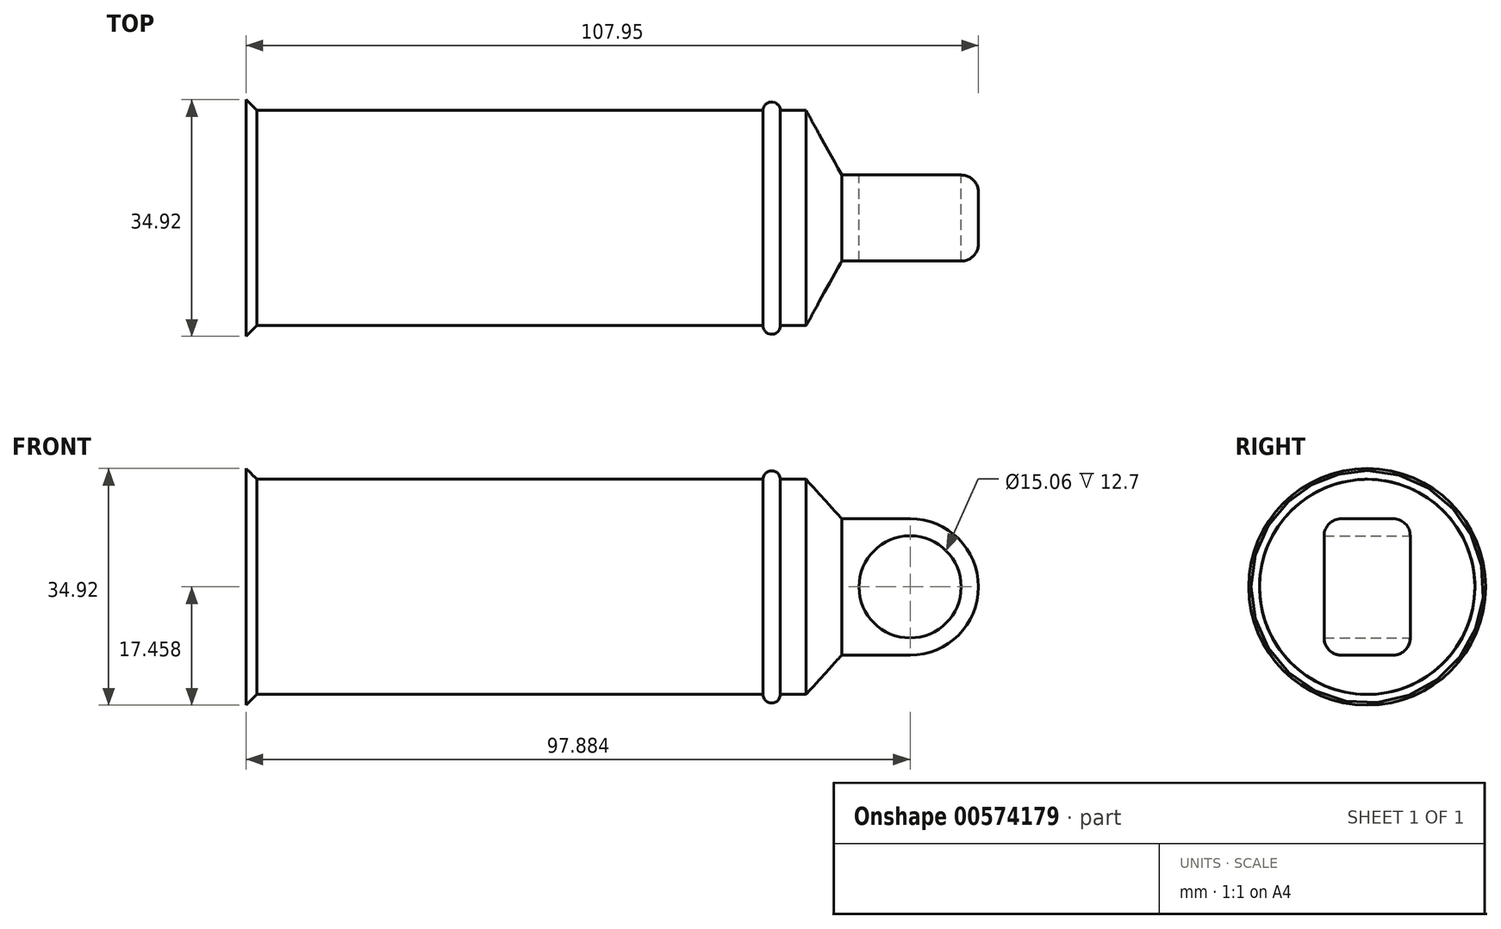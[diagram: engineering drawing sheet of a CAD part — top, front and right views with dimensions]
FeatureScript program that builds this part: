
annotation { "Feature Type Name" : "Feature", "Feature Type Description" : "" }
export const myFeature = defineFeature(function(context is Context, id is Id, definition is map)
    precondition{}
    {
        {
            var Q0;
            Q0=qCreatedBy(makeId("Front.planeOp"),FACE);
            var sketch = newSketch(context, id + "F0", { "sketchPlane" : qUnion([Q0])});
            skLineSegment(sketch, "E0", {"start": v(-107.03, -17.15) * mm, "end": v(134.27, -17.15) * mm, "construction": true});
            skCircle(sketch, "E1", {"center": v(-107.03, -17.15) * mm, "radius": 7.53 * mm});
            skCircle(sketch, "E2", {"center": v(134.27, -17.15) * mm, "radius": 7.53 * mm});
            skArc(sketch, "E3.0", {"start": v(-112.09, -8.45) * mm, "mid": v(-117.1, -17.15) * mm, "end": v(-112.09, -25.86) * mm});
            skArc(sketch, "E4.0", {"start": v(134.27, -27.22) * mm, "mid": v(144.34, -17.15) * mm, "end": v(134.27, -7.08) * mm});
            skLineSegment(sketch, "E5", {"start": v(134.27, -7.08) * mm, "end": v(118.94, -7.08) * mm});
            skLineSegment(sketch, "E6", {"start": v(118.94, -17.15) * mm, "end": v(118.94, -1.28) * mm});
            skLineSegment(sketch, "E7", {"start": v(118.94, -1.28) * mm, "end": v(115.13, -1.28) * mm});
            skLineSegment(sketch, "E8", {"start": v(36.4, -1.28) * mm, "end": v(36.4, -17.15) * mm});
            skLineSegment(sketch, "E9", {"start": v(115.13, -0.97) * mm, "end": v(115.13, -1.28) * mm});
            skLineSegment(sketch, "E10", {"start": v(112.6, -1.28) * mm, "end": v(112.6, -0.97) * mm});
            skLineSegment(sketch, "E11.trimOffspring", {"start": v(112.6, -1.28) * mm, "end": v(37.98, -1.28) * mm});
            skLineSegment(sketch, "E12", {"start": v(36.4, -1.28) * mm, "end": v(36.4, 1.9) * mm});
            skLineSegment(sketch, "E13", {"start": v(35.12, 1.9) * mm, "end": v(27.44, 1.9) * mm});
            skLineSegment(sketch, "E14", {"start": v(27.44, 1.9) * mm, "end": v(27.44, 4.44) * mm});
            skLineSegment(sketch, "E15", {"start": v(27.44, 4.44) * mm, "end": v(-53.08, 4.44) * mm});
            skLineSegment(sketch, "E16", {"start": v(-53.08, 4.44) * mm, "end": v(-53.08, 9.26) * mm});
            skLineSegment(sketch, "E17", {"start": v(-53.08, 9.26) * mm, "end": v(-81.63, 9.26) * mm});
            skLineSegment(sketch, "E18", {"start": v(36.4, 3.17) * mm, "end": v(36.4, 1.9) * mm});
            skPoint(sketch, "E18.startSnap0", {"position": v(27.44, 3.17) * mm});
            skLineSegment(sketch, "E19", {"start": v(36.4, 3.17) * mm, "end": v(35.12, 3.17) * mm});
            skLineSegment(sketch, "E20", {"start": v(35.12, 3.17) * mm, "end": v(35.12, 1.9) * mm});
            skLineSegment(sketch, "E21", {"start": v(36.4, 0.31) * mm, "end": v(37.98, -1.28) * mm});
            skArc(sketch, "E22", {"start": v(115.13, -1.28) * mm, "mid": v(113.86, 0) * mm, "end": v(112.6, -1.28) * mm});
            skLineSegment(sketch, "E23", {"start": v(-81.63, 9.26) * mm, "end": v(-81.63, -17.15) * mm});
            skPoint(sketch, "E24.orphan", {"position": v(35.12, -17.15) * mm});
            skLineSegment(sketch, "E25", {"start": v(-81.63, -17.15) * mm, "end": v(118.94, -17.15) * mm});
            skLineSegment(sketch, "E26.MirrorCS", {"start": v(-81.63, -43.57) * mm, "end": v(-112.09, -25.86) * mm});
            skLineSegment(sketch, "E27", {"start": v(-144.77, 24.76) * mm, "end": v(-96.86, 24.76) * mm, "construction": true});
            skLineSegment(sketch, "E28", {"start": v(-112.09, -8.45) * mm, "end": v(-96.86, 24.76) * mm});
            skPoint(sketch, "E28.endSnap0", {"position": v(-96.86, 0.4) * mm});
            skLineSegment(sketch, "E29", {"start": v(-96.86, 24.76) * mm, "end": v(-96.86, 40) * mm});
            skLineSegment(sketch, "E30", {"start": v(-96.86, 40) * mm, "end": v(10.63, 40) * mm});
            skLineSegment(sketch, "E31", {"start": v(10.63, 40) * mm, "end": v(10.63, 24.76) * mm});
            skLineSegment(sketch, "E32", {"start": v(10.63, 24.76) * mm, "end": v(-69.38, 24.76) * mm});
            skLineSegment(sketch, "E33", {"start": v(-69.38, 9.26) * mm, "end": v(-69.38, 40) * mm});
            skLineSegment(sketch, "E34.trimOffspring", {"start": v(-69.38, 24.76) * mm, "end": v(29.6, 24.76) * mm, "construction": true});
            skLineSegment(sketch, "E35", {"start": v(-69.38, 9.26) * mm, "end": v(-81.63, 9.26) * mm});
            skLineSegment(sketch, "E36", {"start": v(-81.63, -17.15) * mm, "end": v(-81.63, -43.57) * mm});
            skLineSegment(sketch, "E37", {"start": v(-69.38, 9.26) * mm, "end": v(-69.38, -17.15) * mm});
            skPoint(sketch, "E38.start.orphan", {"position": v(-69.38, -43.57) * mm});
            skLineSegment(sketch, "E39.MirrorCS", {"start": v(10.63, 9.52) * mm, "end": v(10.63, 24.76) * mm});
            skLineSegment(sketch, "E40.MirrorCS", {"start": v(-96.86, 9.52) * mm, "end": v(10.63, 9.52) * mm});
            skLineSegment(sketch, "E41", {"start": v(124.2, -17.15) * mm, "end": v(124.2, -7.08) * mm});
            skLineSegment(sketch, "E42.MirrorCS", {"start": v(134.27, -27.22) * mm, "end": v(118.94, -27.22) * mm});
            skLineSegment(sketch, "E43.MirrorCS", {"start": v(124.2, -17.15) * mm, "end": v(124.2, -27.22) * mm});
            skLineSegment(sketch, "E44.MirrorCS", {"start": v(118.94, -17.15) * mm, "end": v(118.94, -33.03) * mm});
            skSolve(sketch);
        }
        {
            var Q0;
            {var subQ1=sQuery(id+"F0.wireOp",EDGE,"E7");Q0=makeQuery(id+"F0.imprint","IMPRINT",FACE,{"disambiguationData":[TD([[makeQuery(id+"F0.imprint","IMPRINT",EDGE,{"derivedFrom":subQ1}),1.0]])]});}
            var Q1;
            Q1=sQuery(id+"F0.wireOp",EDGE,"E0");
            revolve(context, id + "F1", {"entities" : qUnion([Q0]), "axis" : qUnion([Q1]), "revolveType" : RevolveType.FULL});
        }
        {
            var Q0;
            Q0=makeQuery(id+"F0.imprint","IMPRINT",FACE,{"disambiguationData":[TD([[makeQuery(id+"F0.imprint","IMPRINT",EDGE,{"derivedFrom":sQuery(id+"F0.wireOp",EDGE,"E2")}),-1.0]])]});
            extrude(context, id + "F2", {"entities" : qUnion([Q0]), "depth" : 12.7 * mm, "offsetDistance" : 25.4 * mm, "symmetric" : true});
        }
        {
            var Q0;
            Q0=makeQuery(id+"F2.opExtrude","CAP_EDGE",EDGE,{"disambiguationData":[OSD([sQuery(id+"F0.wireOp",EDGE,"E5")])],"isStart":false});
            var Q1;
            Q1=makeQuery(id+"F2.opExtrude","CAP_EDGE",EDGE,{"disambiguationData":[OSD([sQuery(id+"F0.wireOp",EDGE,"E5")])],"isStart":true});
            fillet(context, id + "F3", {"entities" : qUnion([Q0, Q1]), "radius" : 2.54 * mm, "tangentPropagation" : true, "allowEdgeOverflow" : false});
        }
        {
            var Q1;
            Q1=makeQuery(id+"F1.opRevolve","SWEPT_FACE",FACE,{"disambiguationData":[OSD([sQuery(id+"F0.wireOp",EDGE,"E6")])]});
            var Q2;
            Q2=makeQuery(id+"F2.opExtrude","SWEPT_FACE",FACE,{"disambiguationData":[OSD([sQuery(id+"F0.wireOp",EDGE,"E41"),sQuery(id+"F0.wireOp",EDGE,"E43.MirrorCS")])]});
            loft(context, id + "F4", {"operationType" : NewBodyOperationType.ADD, "sheetProfilesArray" : [{ "sheetProfileEntities" : qUnion([Q1]) }, { "sheetProfileEntities" : qUnion([Q2]) }]});
        }
    });
